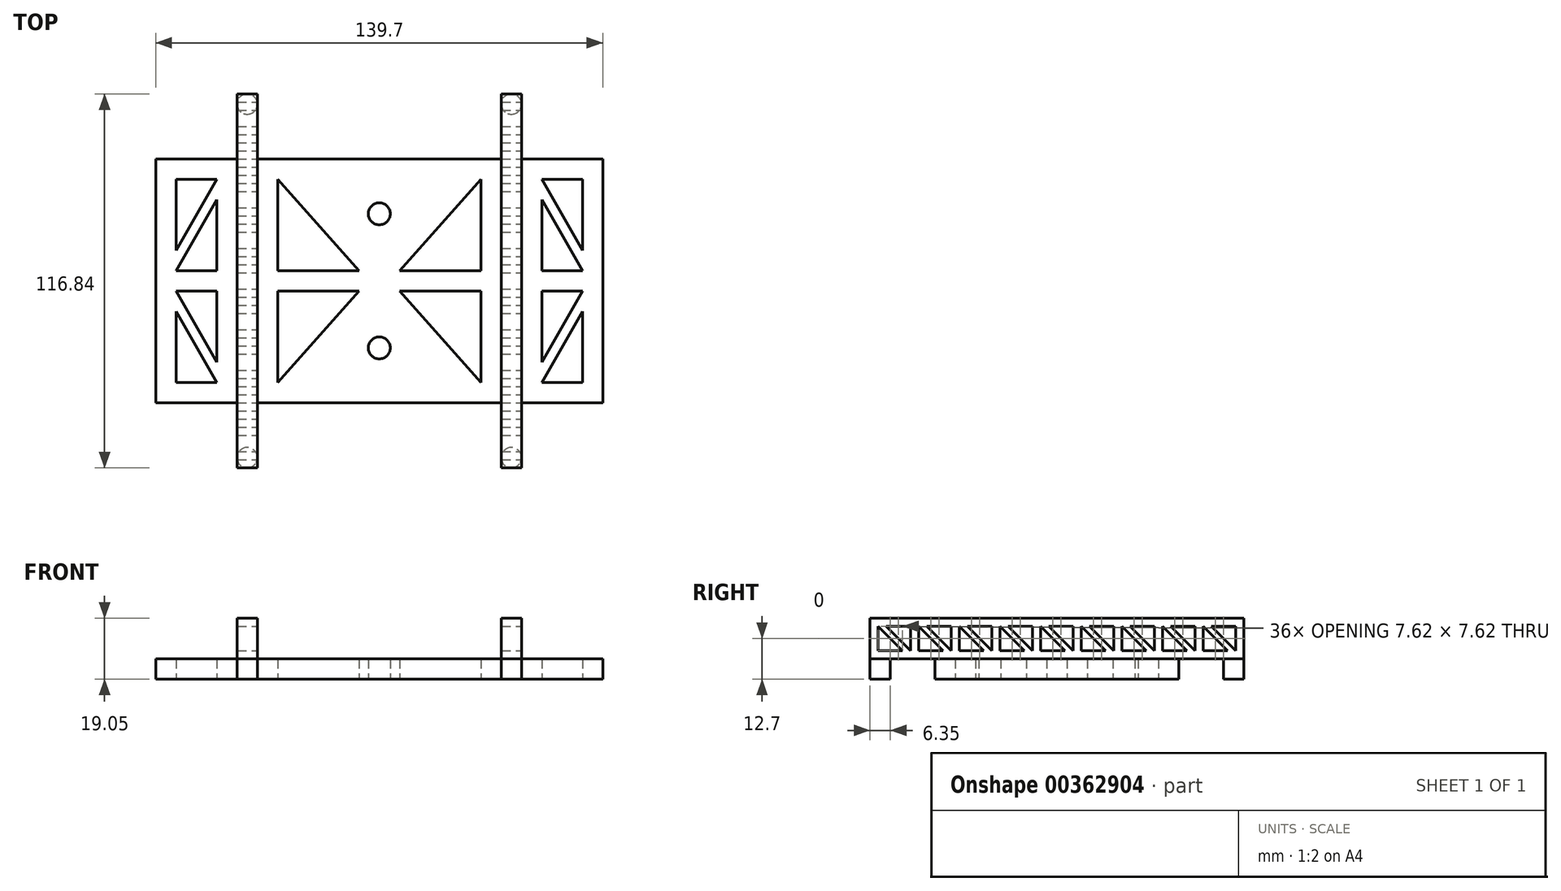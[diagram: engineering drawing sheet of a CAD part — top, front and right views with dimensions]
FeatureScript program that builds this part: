
annotation { "Feature Type Name" : "Feature", "Feature Type Description" : "" }
export const myFeature = defineFeature(function(context is Context, id is Id, definition is map)
    precondition{}
    {
        {
            var Q0;
            Q0=qCreatedBy(makeId("Top.planeOp"),FACE);
            var sketch = newSketch(context, id + "F0", { "sketchPlane" : qUnion([Q0])});
            skLineSegment(sketch, "E0.bottom", {"start": v(-69.85, 38.1) * mm, "end": v(69.85, 38.1) * mm});
            skLineSegment(sketch, "E0.top", {"start": v(-69.85, -38.1) * mm, "end": v(69.85, -38.1) * mm});
            skLineSegment(sketch, "E0.left", {"start": v(-69.85, 38.1) * mm, "end": v(-69.85, -38.1) * mm});
            skLineSegment(sketch, "E0.right", {"start": v(69.85, 38.1) * mm, "end": v(69.85, -38.1) * mm});
            skPoint(sketch, "E0.middle", {"position": v(0, 0) * mm});
            skCircle(sketch, "E1", {"center": v(0, -20.95) * mm, "radius": 3.43 * mm});
            skCircle(sketch, "E2", {"center": v(0, 20.95) * mm, "radius": 3.43 * mm});
            skPoint(sketch, "E2.centerSnap0", {"position": v(0, 38.1) * mm});
            skLineSegment(sketch, "E3", {"start": v(-63.5, 9.52) * mm, "end": v(-63.5, 31.75) * mm});
            skLineSegment(sketch, "E4", {"start": v(-63.5, 31.75) * mm, "end": v(-50.8, 31.75) * mm});
            skLineSegment(sketch, "E5", {"start": v(-50.8, 31.75) * mm, "end": v(-63.5, 9.52) * mm});
            skLineSegment(sketch, "E6", {"start": v(-50.8, 3.17) * mm, "end": v(-50.8, 25.4) * mm});
            skLineSegment(sketch, "E7", {"start": v(-50.8, 25.4) * mm, "end": v(-63.5, 3.17) * mm});
            skLineSegment(sketch, "E8", {"start": v(-63.5, 3.17) * mm, "end": v(-50.8, 3.17) * mm});
            skLineSegment(sketch, "E9.MirrorCS", {"start": v(-63.5, -3.17) * mm, "end": v(-50.8, -3.17) * mm});
            skLineSegment(sketch, "E10.MirrorCS", {"start": v(-50.8, -3.17) * mm, "end": v(-50.8, -25.4) * mm});
            skLineSegment(sketch, "E11.MirrorCS", {"start": v(-50.8, -25.4) * mm, "end": v(-63.5, -3.17) * mm});
            skLineSegment(sketch, "E12.MirrorCS", {"start": v(-50.8, -31.75) * mm, "end": v(-63.5, -9.52) * mm});
            skLineSegment(sketch, "E13.MirrorCS", {"start": v(-63.5, -31.75) * mm, "end": v(-50.8, -31.75) * mm});
            skLineSegment(sketch, "E14.MirrorCS", {"start": v(-63.5, -9.52) * mm, "end": v(-63.5, -31.75) * mm});
            skLineSegment(sketch, "E15.MirrorCS", {"start": v(50.8, 3.17) * mm, "end": v(50.8, 25.4) * mm});
            skLineSegment(sketch, "E16.MirrorCS", {"start": v(50.8, 25.4) * mm, "end": v(63.5, 3.17) * mm});
            skLineSegment(sketch, "E17.MirrorCS", {"start": v(63.5, 3.17) * mm, "end": v(50.8, 3.17) * mm});
            skLineSegment(sketch, "E18.MirrorCS", {"start": v(50.8, 31.75) * mm, "end": v(63.5, 9.52) * mm});
            skLineSegment(sketch, "E19.MirrorCS", {"start": v(63.5, 9.52) * mm, "end": v(63.5, 31.75) * mm});
            skLineSegment(sketch, "E20.MirrorCS", {"start": v(63.5, 31.75) * mm, "end": v(50.8, 31.75) * mm});
            skLineSegment(sketch, "E21.MirrorCS", {"start": v(50.8, -25.4) * mm, "end": v(63.5, -3.17) * mm});
            skLineSegment(sketch, "E22.MirrorCS", {"start": v(63.5, -3.17) * mm, "end": v(50.8, -3.17) * mm});
            skLineSegment(sketch, "E23.MirrorCS", {"start": v(50.8, -3.17) * mm, "end": v(50.8, -25.4) * mm});
            skLineSegment(sketch, "E24.MirrorCS", {"start": v(63.5, -9.52) * mm, "end": v(63.5, -31.75) * mm});
            skLineSegment(sketch, "E25.MirrorCS", {"start": v(50.8, -31.75) * mm, "end": v(63.5, -9.52) * mm});
            skLineSegment(sketch, "E26.MirrorCS", {"start": v(63.5, -31.75) * mm, "end": v(50.8, -31.75) * mm});
            skLineSegment(sketch, "E27", {"start": v(-31.75, 3.17) * mm, "end": v(-31.75, 31.75) * mm});
            skLineSegment(sketch, "E28", {"start": v(-31.75, 31.75) * mm, "end": v(-6.35, 3.17) * mm});
            skLineSegment(sketch, "E29", {"start": v(-6.35, 3.17) * mm, "end": v(-31.75, 3.17) * mm});
            skLineSegment(sketch, "E30", {"start": v(-31.75, -3.17) * mm, "end": v(-31.75, -31.75) * mm});
            skLineSegment(sketch, "E31", {"start": v(-31.75, -31.75) * mm, "end": v(-6.35, -3.17) * mm});
            skLineSegment(sketch, "E32", {"start": v(-6.35, -3.17) * mm, "end": v(-31.75, -3.17) * mm});
            skLineSegment(sketch, "E33.MirrorCS", {"start": v(31.75, 31.75) * mm, "end": v(6.35, 3.17) * mm});
            skLineSegment(sketch, "E34.MirrorCS", {"start": v(31.75, 3.17) * mm, "end": v(31.75, 31.75) * mm});
            skLineSegment(sketch, "E35.MirrorCS", {"start": v(6.35, 3.17) * mm, "end": v(31.75, 3.17) * mm});
            skLineSegment(sketch, "E36.MirrorCS", {"start": v(6.35, -3.17) * mm, "end": v(31.75, -3.17) * mm});
            skLineSegment(sketch, "E37.MirrorCS", {"start": v(31.75, -3.17) * mm, "end": v(31.75, -31.75) * mm});
            skLineSegment(sketch, "E38.MirrorCS", {"start": v(31.75, -31.75) * mm, "end": v(6.35, -3.17) * mm});
            skSolve(sketch);
        }
        {
            var Q0;
            Q0=makeQuery(id+"F0.imprint","IMPRINT",FACE,{"disambiguationData":[TD([[makeQuery(id+"F0.imprint","IMPRINT",EDGE,{"derivedFrom":sQuery(id+"F0.wireOp",EDGE,"E0.bottom")}),-1.0]])]});
            extrude(context, id + "F1", {"entities" : qUnion([Q0]), "depth" : 6.35 * mm});
        }
        {
            var Q0;
            Q0=makeQuery(id+"F1.opExtrude","CAP_FACE",FACE,{"disambiguationData":[OSD([sQuery(id+"F0.wireOp",EDGE,"E0.bottom"),sQuery(id+"F0.wireOp",EDGE,"E0.top"),sQuery(id+"F0.wireOp",EDGE,"E0.left"),sQuery(id+"F0.wireOp",EDGE,"E0.right")])],"isStart":false});
            var sketch = newSketch(context, id + "F2", { "sketchPlane" : qUnion([Q0])});
            skLineSegment(sketch, "E39.bottom", {"start": v(38.1, 58.42) * mm, "end": v(44.45, 58.42) * mm});
            skLineSegment(sketch, "E39.top", {"start": v(38.1, -58.42) * mm, "end": v(44.45, -58.42) * mm});
            skLineSegment(sketch, "E39.left", {"start": v(38.1, 58.42) * mm, "end": v(38.1, -58.42) * mm});
            skLineSegment(sketch, "E39.right", {"start": v(44.45, 58.42) * mm, "end": v(44.45, -58.42) * mm});
            skPoint(sketch, "E39.middle", {"position": v(41.28, 0) * mm});
            skLineSegment(sketch, "E40", {"start": v(0, 55.36) * mm, "end": v(0, -69.96) * mm, "construction": true});
            skLineSegment(sketch, "E41.MirrorCS", {"start": v(-38.1, 58.42) * mm, "end": v(-38.1, -58.42) * mm});
            skLineSegment(sketch, "E42.MirrorCS", {"start": v(-44.45, 58.42) * mm, "end": v(-44.45, -58.42) * mm});
            skLineSegment(sketch, "E43.MirrorCS", {"start": v(-38.1, -58.42) * mm, "end": v(-44.45, -58.42) * mm});
            skLineSegment(sketch, "E44.MirrorCS", {"start": v(-38.1, 58.42) * mm, "end": v(-44.45, 58.42) * mm});
            skSolve(sketch);
        }
        {
            var Q0;
            {var subQ0=sQuery(id+"F2.wireOp",EDGE,"04U5UkVg-AJ8Z-mwcw-HsoT-IvXdQoQTUmTr.bottom");Q0=makeQuery(id+"F2.imprint","IMPRINT",FACE,{"disambiguationData":[TD([[makeQuery(id+"F2.imprint","IMPRINT",EDGE,{"derivedFrom":subQ0}),-1.0]])]});}
            var Q1;
            {var subQ0=sQuery(id+"F2.wireOp",EDGE,"04U5UkVg-AJ8Z-mwcw-HsoT-IvXdQoQTUmTr.left");var subQ1=makeQuery(id+"F1.opExtrude","CAP_EDGE",EDGE,{"disambiguationData":[OSD([sQuery(id+"F0.wireOp",EDGE,"E0.bottom")])],"isStart":false});var subQ2=makeQuery(id+"F2.imprint","INTERSECT",VERTEX,{"derivedFrom":[subQ1,subQ0]});Q1=makeQuery(id+"F2.imprint","IMPRINT",FACE,{"disambiguationData":[TD([[makeQuery(id+"F2.imprint","IMPRINT",EDGE,{"disambiguationData":[TD([[subQ2,-1.0]])],"derivedFrom":subQ0}),1.0]])]});}
            var Q2;
            {var subQ0=sQuery(id+"F2.wireOp",EDGE,"04U5UkVg-AJ8Z-mwcw-HsoT-IvXdQoQTUmTr.top");Q2=makeQuery(id+"F2.imprint","IMPRINT",FACE,{"disambiguationData":[TD([[makeQuery(id+"F2.imprint","IMPRINT",EDGE,{"derivedFrom":subQ0}),1.0]])]});}
            var Q3;
            {var subQ0=sQuery(id+"F2.wireOp",EDGE,"E39.top");Q3=makeQuery(id+"F2.imprint","IMPRINT",FACE,{"disambiguationData":[TD([[makeQuery(id+"F2.imprint","IMPRINT",EDGE,{"derivedFrom":subQ0}),1.0]])]});}
            var Q4;
            {var subQ0=sQuery(id+"F2.wireOp",EDGE,"E39.left");var subQ1=makeQuery(id+"F1.opExtrude","CAP_EDGE",EDGE,{"disambiguationData":[OSD([sQuery(id+"F0.wireOp",EDGE,"E0.bottom")])],"isStart":false});var subQ2=makeQuery(id+"F2.imprint","INTERSECT",VERTEX,{"derivedFrom":[subQ1,subQ0]});Q4=makeQuery(id+"F2.imprint","IMPRINT",FACE,{"disambiguationData":[TD([[makeQuery(id+"F2.imprint","IMPRINT",EDGE,{"disambiguationData":[TD([[subQ2,-1.0]])],"derivedFrom":subQ0}),1.0]])]});}
            var Q5;
            {var subQ0=sQuery(id+"F2.wireOp",EDGE,"E39.bottom");Q5=makeQuery(id+"F2.imprint","IMPRINT",FACE,{"disambiguationData":[TD([[makeQuery(id+"F2.imprint","IMPRINT",EDGE,{"derivedFrom":subQ0}),-1.0]])]});}
            var Q6;
            {var subQ0=sQuery(id+"F2.wireOp",EDGE,"E44.MirrorCS");Q6=makeQuery(id+"F2.imprint","IMPRINT",FACE,{"disambiguationData":[TD([[makeQuery(id+"F2.imprint","IMPRINT",EDGE,{"derivedFrom":subQ0}),1.0]])]});}
            var Q7;
            {var subQ0=sQuery(id+"F2.wireOp",EDGE,"E41.MirrorCS");var subQ1=makeQuery(id+"F1.opExtrude","CAP_EDGE",EDGE,{"disambiguationData":[OSD([sQuery(id+"F0.wireOp",EDGE,"E0.bottom")])],"isStart":false});var subQ2=makeQuery(id+"F2.imprint","INTERSECT",VERTEX,{"derivedFrom":[subQ1,subQ0]});Q7=makeQuery(id+"F2.imprint","IMPRINT",FACE,{"disambiguationData":[TD([[makeQuery(id+"F2.imprint","IMPRINT",EDGE,{"disambiguationData":[TD([[subQ2,-1.0]])],"derivedFrom":subQ0}),-1.0]])]});}
            var Q8;
            {var subQ0=sQuery(id+"F2.wireOp",EDGE,"E43.MirrorCS");Q8=makeQuery(id+"F2.imprint","IMPRINT",FACE,{"disambiguationData":[TD([[makeQuery(id+"F2.imprint","IMPRINT",EDGE,{"derivedFrom":subQ0}),-1.0]])]});}
            extrude(context, id + "F3", {"entities" : qUnion([Q0, Q1, Q2, Q3, Q4, Q5, Q6, Q7, Q8]), "operationType" : NewBodyOperationType.ADD, "depth" : 12.7 * mm});
        }
        {
            var Q0;
            Q0=makeQuery(id+"F3.opExtrude","SWEPT_FACE",FACE,{"disambiguationData":[OSD([sQuery(id+"F2.wireOp",EDGE,"E39.right")])]});
            var sketch = newSketch(context, id + "F4", { "sketchPlane" : qUnion([Q0])});
            skLineSegment(sketch, "E45", {"start": v(-55.88, 16.51) * mm, "end": v(-55.88, 8.9) * mm});
            skLineSegment(sketch, "E46", {"start": v(-55.88, 8.9) * mm, "end": v(-48.26, 8.9) * mm});
            skLineSegment(sketch, "E47", {"start": v(-48.26, 8.9) * mm, "end": v(-55.88, 16.51) * mm});
            skLineSegment(sketch, "E48", {"start": v(-53.34, 16.51) * mm, "end": v(-45.72, 8.9) * mm});
            skLineSegment(sketch, "E49", {"start": v(-45.72, 8.9) * mm, "end": v(-45.72, 16.51) * mm});
            skLineSegment(sketch, "E50", {"start": v(-45.72, 16.51) * mm, "end": v(-53.34, 16.51) * mm});
            skLineSegment(sketch, "E51.1.0.0", {"start": v(-33.02, 8.89) * mm, "end": v(-33.02, 16.51) * mm});
            skLineSegment(sketch, "E51.1.0.1", {"start": v(-40.64, 16.51) * mm, "end": v(-33.02, 8.9) * mm});
            skLineSegment(sketch, "E51.1.0.2", {"start": v(-33.02, 16.51) * mm, "end": v(-40.64, 16.51) * mm});
            skLineSegment(sketch, "E51.1.0.3", {"start": v(-35.56, 8.9) * mm, "end": v(-43.18, 16.51) * mm});
            skLineSegment(sketch, "E51.1.0.4", {"start": v(-43.18, 16.5) * mm, "end": v(-43.18, 8.9) * mm});
            skLineSegment(sketch, "E51.1.0.5", {"start": v(-43.18, 8.9) * mm, "end": v(-35.56, 8.9) * mm});
            skLineSegment(sketch, "E51.2.0.0", {"start": v(-20.32, 8.89) * mm, "end": v(-20.32, 16.51) * mm});
            skLineSegment(sketch, "E51.2.0.1", {"start": v(-27.94, 16.51) * mm, "end": v(-20.32, 8.9) * mm});
            skLineSegment(sketch, "E51.2.0.2", {"start": v(-20.32, 16.51) * mm, "end": v(-27.94, 16.51) * mm});
            skLineSegment(sketch, "E51.2.0.3", {"start": v(-22.86, 8.89) * mm, "end": v(-30.48, 16.5) * mm});
            skLineSegment(sketch, "E51.2.0.4", {"start": v(-30.48, 16.5) * mm, "end": v(-30.48, 8.89) * mm});
            skLineSegment(sketch, "E51.2.0.5", {"start": v(-30.48, 8.9) * mm, "end": v(-22.86, 8.9) * mm});
            skLineSegment(sketch, "E51.3.0.0", {"start": v(-7.62, 8.89) * mm, "end": v(-7.62, 16.5) * mm});
            skLineSegment(sketch, "E51.3.0.1", {"start": v(-15.24, 16.51) * mm, "end": v(-7.62, 8.89) * mm});
            skLineSegment(sketch, "E51.3.0.2", {"start": v(-7.62, 16.51) * mm, "end": v(-15.24, 16.51) * mm});
            skLineSegment(sketch, "E51.3.0.3", {"start": v(-10.16, 8.9) * mm, "end": v(-17.78, 16.51) * mm});
            skLineSegment(sketch, "E51.3.0.4", {"start": v(-17.78, 16.5) * mm, "end": v(-17.78, 8.89) * mm});
            skLineSegment(sketch, "E51.3.0.5", {"start": v(-17.78, 8.9) * mm, "end": v(-10.16, 8.9) * mm});
            skLineSegment(sketch, "E51.4.0.0", {"start": v(5.08, 8.89) * mm, "end": v(5.08, 16.5) * mm});
            skLineSegment(sketch, "E51.4.0.1", {"start": v(-2.54, 16.51) * mm, "end": v(5.08, 8.89) * mm});
            skLineSegment(sketch, "E51.4.0.2", {"start": v(5.08, 16.51) * mm, "end": v(-2.54, 16.51) * mm});
            skLineSegment(sketch, "E51.4.0.3", {"start": v(2.54, 8.89) * mm, "end": v(-5.08, 16.5) * mm});
            skLineSegment(sketch, "E51.4.0.4", {"start": v(-5.08, 16.5) * mm, "end": v(-5.08, 8.89) * mm});
            skLineSegment(sketch, "E51.4.0.5", {"start": v(-5.08, 8.9) * mm, "end": v(2.54, 8.9) * mm});
            skLineSegment(sketch, "E51.5.0.0", {"start": v(17.78, 8.89) * mm, "end": v(17.78, 16.5) * mm});
            skLineSegment(sketch, "E51.5.0.1", {"start": v(10.16, 16.51) * mm, "end": v(17.78, 8.89) * mm});
            skLineSegment(sketch, "E51.5.0.2", {"start": v(17.78, 16.51) * mm, "end": v(10.16, 16.51) * mm});
            skLineSegment(sketch, "E51.5.0.3", {"start": v(15.24, 8.89) * mm, "end": v(7.62, 16.5) * mm});
            skLineSegment(sketch, "E51.5.0.4", {"start": v(7.62, 16.5) * mm, "end": v(7.62, 8.89) * mm});
            skLineSegment(sketch, "E51.5.0.5", {"start": v(7.62, 8.9) * mm, "end": v(15.24, 8.9) * mm});
            skLineSegment(sketch, "E51.6.0.0", {"start": v(30.48, 8.89) * mm, "end": v(30.48, 16.5) * mm});
            skLineSegment(sketch, "E51.6.0.1", {"start": v(22.86, 16.51) * mm, "end": v(30.48, 8.89) * mm});
            skLineSegment(sketch, "E51.6.0.2", {"start": v(30.48, 16.51) * mm, "end": v(22.86, 16.51) * mm});
            skLineSegment(sketch, "E51.6.0.3", {"start": v(27.94, 8.89) * mm, "end": v(20.32, 16.5) * mm});
            skLineSegment(sketch, "E51.6.0.4", {"start": v(20.32, 16.5) * mm, "end": v(20.32, 8.89) * mm});
            skLineSegment(sketch, "E51.6.0.5", {"start": v(20.32, 8.9) * mm, "end": v(27.94, 8.9) * mm});
            skLineSegment(sketch, "E51.7.0.0", {"start": v(43.18, 8.89) * mm, "end": v(43.18, 16.5) * mm});
            skLineSegment(sketch, "E51.7.0.1", {"start": v(35.56, 16.51) * mm, "end": v(43.18, 8.89) * mm});
            skLineSegment(sketch, "E51.7.0.2", {"start": v(43.18, 16.51) * mm, "end": v(35.56, 16.51) * mm});
            skLineSegment(sketch, "E51.7.0.3", {"start": v(40.64, 8.89) * mm, "end": v(33.02, 16.5) * mm});
            skLineSegment(sketch, "E51.7.0.4", {"start": v(33.02, 16.5) * mm, "end": v(33.02, 8.89) * mm});
            skLineSegment(sketch, "E51.7.0.5", {"start": v(33.02, 8.9) * mm, "end": v(40.64, 8.9) * mm});
            skLineSegment(sketch, "E51.8.0.0", {"start": v(55.88, 8.89) * mm, "end": v(55.88, 16.5) * mm});
            skLineSegment(sketch, "E51.8.0.1", {"start": v(48.26, 16.51) * mm, "end": v(55.88, 8.89) * mm});
            skLineSegment(sketch, "E51.8.0.2", {"start": v(55.88, 16.51) * mm, "end": v(48.26, 16.51) * mm});
            skLineSegment(sketch, "E51.8.0.3", {"start": v(53.34, 8.89) * mm, "end": v(45.72, 16.5) * mm});
            skLineSegment(sketch, "E51.8.0.4", {"start": v(45.72, 16.5) * mm, "end": v(45.72, 8.89) * mm});
            skLineSegment(sketch, "E51.8.0.5", {"start": v(45.72, 8.9) * mm, "end": v(53.34, 8.9) * mm});
            skLineSegment(sketch, "E51.direction1", {"start": v(-45.72, 8.9) * mm, "end": v(-33.02, 8.9) * mm, "construction": true});
            skSolve(sketch);
        }
        {
            var Q0;
            Q0 = qSketchRegion(id + "F4", true);
            extrude(context, id + "F5", {"entities" : qUnion([Q0]), "operationType" : NewBodyOperationType.REMOVE, "endBound" : BoundingType.THROUGH_ALL, "oppositeDirection" : true, "depth" : 6.35 * mm});
        }
        {
            var Q0;
            {var subQ0=sQuery(id+"F2.wireOp",EDGE,"E41.MirrorCS");var subQ1=sQuery(id+"F0.wireOp",EDGE,"E0.top");var subQ2=sQuery(id+"F2.wireOp",EDGE,"E42.MirrorCS");var subQ3=sQuery(id+"F2.wireOp",EDGE,"E43.MirrorCS");Q0=makeQuery(id+"F3.boolean.opBoolean","SPLIT",FACE,{"disambiguationData":[TD([makeQuery(id+"F1.opExtrude","SWEPT_FACE",FACE,{"disambiguationData":[OSD([subQ1])]})])],"derivedFrom":makeQuery(id+"F3.opExtrude","CAP_FACE",FACE,{"disambiguationData":[OSD([subQ0,subQ2,subQ3,sQuery(id+"F2.wireOp",EDGE,"E44.MirrorCS")])],"isStart":true})});}
            var sketch = newSketch(context, id + "F6", { "sketchPlane" : qUnion([Q0])});
            skCircle(sketch, "E52", {"center": v(-41.28, 55.24) * mm, "radius": 3.18 * mm});
            skCircle(sketch, "E53", {"center": v(41.28, 55.24) * mm, "radius": 3.18 * mm});
            skCircle(sketch, "E54", {"center": v(-41.28, -55.24) * mm, "radius": 3.18 * mm});
            skCircle(sketch, "E55", {"center": v(41.28, -55.24) * mm, "radius": 3.18 * mm});
            skSolve(sketch);
        }
        {
            var Q0;
            {var subQ0=sQuery(id+"F6.wireOp",EDGE,"E52");var subQ1=sQuery(id+"F2.wireOp",EDGE,"E43.MirrorCS");var subQ2=makeQuery(id+"F6.imprint","INTERSECT",VERTEX,{"derivedFrom":[makeQuery(id+"F3.opExtrude","CAP_EDGE",EDGE,{"disambiguationData":[OSD([subQ1])],"isStart":true}),subQ0]});Q0=makeQuery(id+"F6.imprint","IMPRINT",FACE,{"disambiguationData":[TD([[makeQuery(id+"F6.imprint","IMPRINT",EDGE,{"disambiguationData":[TD([[subQ2,1.0]])],"derivedFrom":subQ0}),1.0]])]});}
            var Q1;
            Q1=makeQuery(id+"F6.imprint","IMPRINT",FACE,{"disambiguationData":[TD([[makeQuery(id+"F6.imprint","IMPRINT",EDGE,{"derivedFrom":sQuery(id+"F6.wireOp",EDGE,"E53")}),1.0]])]});
            var Q2;
            Q2=makeQuery(id+"F6.imprint","IMPRINT",FACE,{"disambiguationData":[TD([[makeQuery(id+"F6.imprint","IMPRINT",EDGE,{"derivedFrom":sQuery(id+"F6.wireOp",EDGE,"E54")}),1.0]])]});
            var Q3;
            Q3=makeQuery(id+"F6.imprint","IMPRINT",FACE,{"disambiguationData":[TD([[makeQuery(id+"F6.imprint","IMPRINT",EDGE,{"derivedFrom":sQuery(id+"F6.wireOp",EDGE,"E55")}),1.0]])]});
            extrude(context, id + "F7", {"entities" : qUnion([Q0, Q1, Q2, Q3]), "operationType" : NewBodyOperationType.ADD, "depth" : 6.35 * mm});
        }
    });
